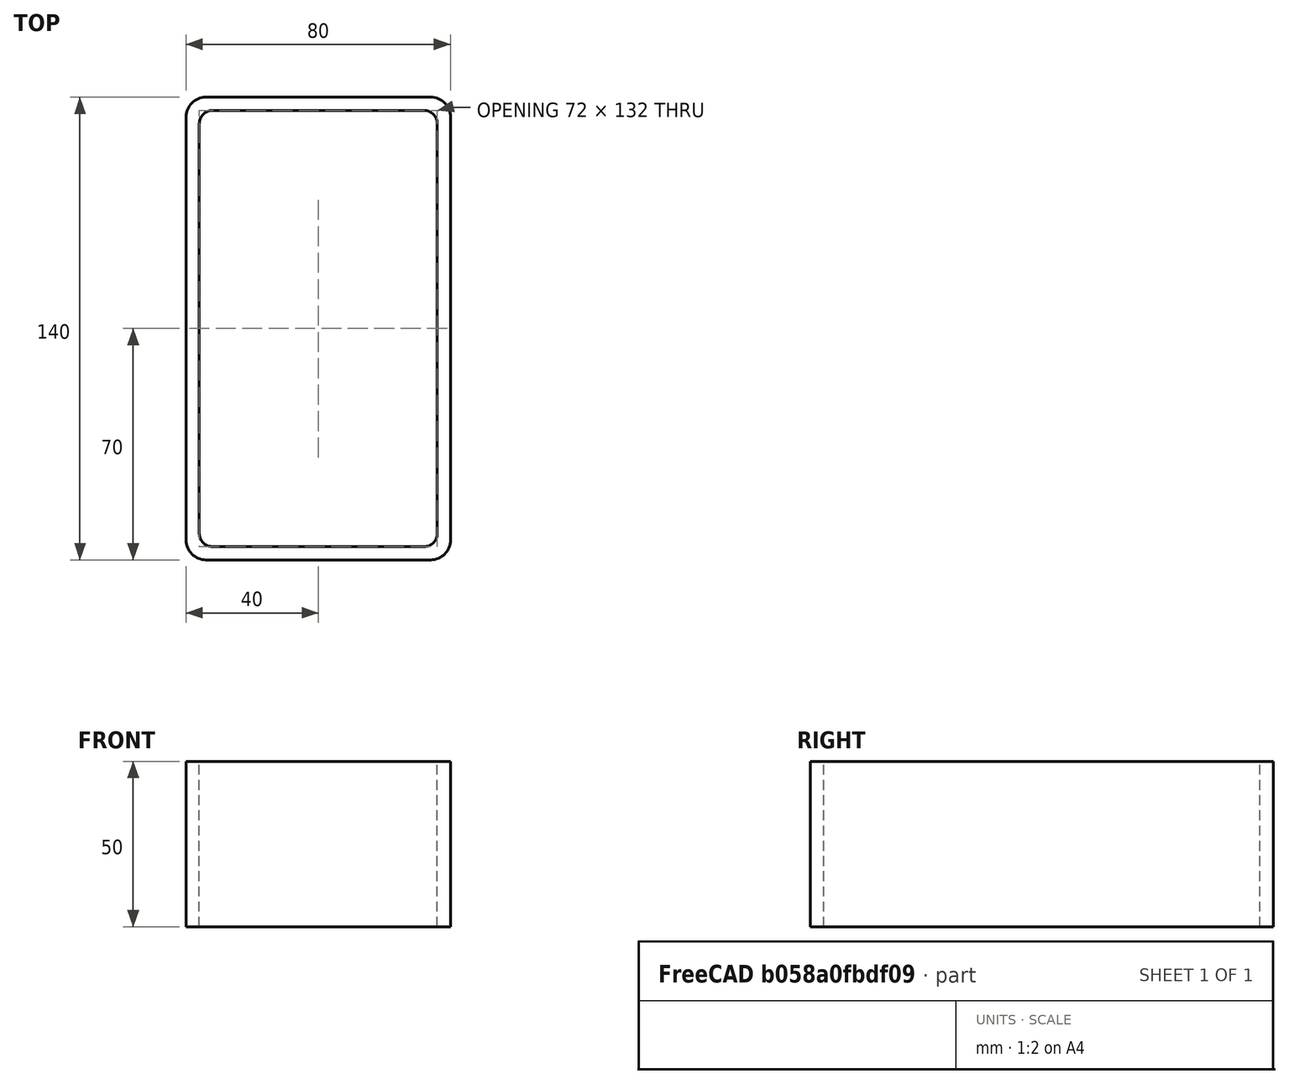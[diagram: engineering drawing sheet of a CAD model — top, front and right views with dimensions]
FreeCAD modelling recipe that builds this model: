
FCSTD DOCUMENT  (FreeCAD 0.15R4671 (Git))
Label: Rectangular hollow section 140x80x4 EN10219 S235JRH
License: All rights reserved
LicenseURL: http://en.wikipedia.org/wiki/All_rights_reserved
objects: Sketcher::SketchObject×1, Part::Extrusion×1
note: 2 computed .brp shape members not serialized (recipe doc carries the construction recipe); baked Part::Feature solids carry a one-line shape summary decoded from their .brp

FEATURE [Sketcher::SketchObject] Sketch
  sketch-geometry (16):
    g0: LineSegment StartX=-32 StartY=66 StartZ=0 EndX=32 EndY=66 EndZ=0
    g1: LineSegment StartX=36 StartY=62 StartZ=0 EndX=36 EndY=-62 EndZ=0
    g2: LineSegment StartX=32 StartY=-66 StartZ=0 EndX=-32 EndY=-66 EndZ=0
    g3: LineSegment StartX=-36 StartY=-62 StartZ=0 EndX=-36 EndY=62 EndZ=0
    g4: LineSegment StartX=-34 StartY=70 StartZ=0 EndX=34 EndY=70 EndZ=0
    g5: LineSegment StartX=40 StartY=64 StartZ=0 EndX=40 EndY=-64 EndZ=0
    g6: LineSegment StartX=34 StartY=-70 StartZ=0 EndX=-34 EndY=-70 EndZ=0
    g7: LineSegment StartX=-40 StartY=-64 StartZ=0 EndX=-40 EndY=64 EndZ=0
    g8: ArcOfCircle CenterX=-32 CenterY=62 CenterZ=0 NormalX=0 NormalY=0 NormalZ=1 Radius=4 StartAngle=1.5708 EndAngle=3.14159
    g9: ArcOfCircle CenterX=32 CenterY=62 CenterZ=0 NormalX=0 NormalY=0 NormalZ=1 Radius=4 StartAngle=0 EndAngle=1.5708
    g10: ArcOfCircle CenterX=32 CenterY=-62 CenterZ=0 NormalX=0 NormalY=0 NormalZ=1 Radius=4 StartAngle=4.71239 EndAngle=6.28319
    g11: ArcOfCircle CenterX=-32 CenterY=-62 CenterZ=0 NormalX=0 NormalY=0 NormalZ=1 Radius=4 StartAngle=3.14159 EndAngle=4.71239
    g12: ArcOfCircle CenterX=34 CenterY=64 CenterZ=0 NormalX=0 NormalY=0 NormalZ=1 Radius=6 StartAngle=0 EndAngle=1.5708
    g13: ArcOfCircle CenterX=34 CenterY=-64 CenterZ=0 NormalX=0 NormalY=0 NormalZ=1 Radius=6 StartAngle=4.71239 EndAngle=6.28319
    g14: ArcOfCircle CenterX=-34 CenterY=-64 CenterZ=0 NormalX=0 NormalY=0 NormalZ=1 Radius=6 StartAngle=3.14159 EndAngle=4.71239
    g15: ArcOfCircle CenterX=-34 CenterY=64 CenterZ=0 NormalX=0 NormalY=0 NormalZ=1 Radius=6 StartAngle=1.5708 EndAngle=3.14159
  constraints (36):
    c: Horizontal(g2)
    c: Vertical(g3)
    c: Horizontal(g6)
    c: Vertical(g7)
    c: Tangent(g3,g8) = 1.5708
    c: Tangent(g0,g8) = 1.5708
    c: Tangent(g0,g9) = 1.5708
    c: Tangent(g1,g9) = 1.5708
    c: Tangent(g1,g10) = 1.5708
    c: Tangent(g2,g10) = 1.5708
    c: Tangent(g2,g11) = 1.5708
    c: Tangent(g3,g11) = 1.5708
    c: Tangent(g4,g12) = 1.5708
    c: Tangent(g5,g12) = 1.5708
    c: Tangent(g5,g13) = 1.5708
    c: Tangent(g6,g13) = 1.5708
    c: Tangent(g6,g14) = 1.5708
    c: Tangent(g7,g14) = 1.5708
    c: Tangent(g7,g15) = 1.5708
    c: Tangent(g4,g15) = 1.5708
    c: Equal(g9,g8)
    c: Equal(g9,g11)
    c: Equal(g9,g10)
    c: Equal(g12,g15)
    c: Equal(g12,g14)
    c: Equal(g12,g13)
    c: Symmetric(g4,g6,g-1)
    c: Symmetric(g7,g5,g-2)
    c: DistanceY(g4,g6) = -140
    c: DistanceX(g7,g5) = 80
    c: Symmetric(g3,g1,g-2)
    c: Symmetric(g0,g2,g-1)
    c: DistanceY(g0,g4) = 4
    c: DistanceX(g5,g1) = -4
    c: Radius(g9) = 4
    c: Radius(g12) = 6
FEATURE [Part::Extrusion] Extrude  label="Rectangular hollow section 140x80x4 EN10219 S235JRH"
  Base = -> Sketch
  Dir = (0,0,50)
  Solid = true
